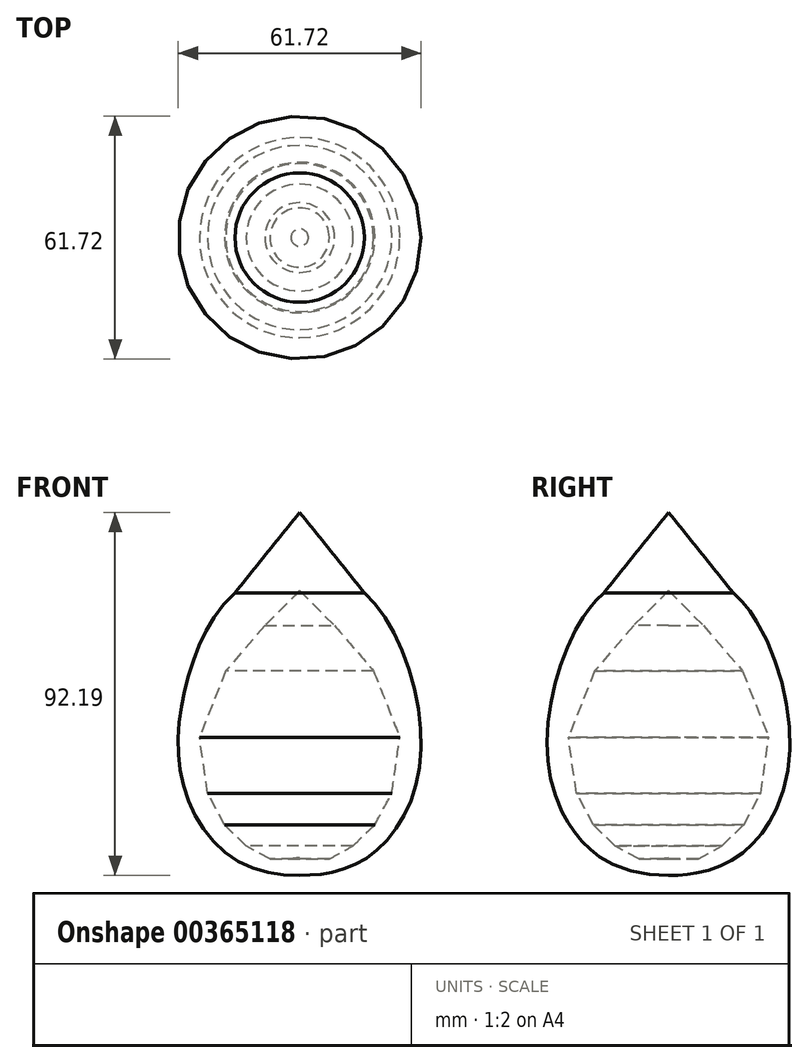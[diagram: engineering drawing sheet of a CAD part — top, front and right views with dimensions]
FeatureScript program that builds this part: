
annotation { "Feature Type Name" : "Feature", "Feature Type Description" : "" }
export const myFeature = defineFeature(function(context is Context, id is Id, definition is map)
    precondition{}
    {
        {
            var Q0;
            Q0=qCreatedBy(makeId("Front.planeOp"),FACE);
            var sketch = newSketch(context, id + "F0", { "sketchPlane" : qUnion([Q0])});
            skFitSpline(sketch, "E0", {"points": [v(-13.57, -42.8) * mm, v(3, -38.67) * mm, v(17.18, -12.44) * mm, v(2.87, 28.92) * mm, v(-13.57, 33.4) * mm], "startDerivative": vector(71.93, -0.04) * mm, "endDerivative": vector(-67.02, -1) * mm});
            skLineSegment(sketch, "E1", {"start": v(-4.72, 20.7) * mm, "end": v(-13.57, 29.55) * mm});
            skLineSegment(sketch, "E2", {"start": v(-13.57, 29.55) * mm, "end": v(-13.57, 33.4) * mm});
            skLineSegment(sketch, "E3", {"start": v(-4.72, 20.7) * mm, "end": v(5.2, 9.15) * mm});
            skLineSegment(sketch, "E4", {"start": v(5.2, 9.15) * mm, "end": v(11.87, -7.69) * mm});
            skLineSegment(sketch, "E5", {"start": v(11.87, -7.69) * mm, "end": v(10.85, -14.84) * mm});
            skLineSegment(sketch, "E6", {"start": v(-13.57, 50.02) * mm, "end": v(-13.57, -55.05) * mm, "construction": true});
            skLineSegment(sketch, "E7", {"start": v(10.85, -14.84) * mm, "end": v(9.84, -21.93) * mm});
            skLineSegment(sketch, "E8", {"start": v(9.84, -21.93) * mm, "end": v(5.52, -29.95) * mm});
            skLineSegment(sketch, "E9", {"start": v(5.52, -29.95) * mm, "end": v(0, -35.28) * mm});
            skLineSegment(sketch, "E10", {"start": v(0, -35.28) * mm, "end": v(-6.03, -38.61) * mm});
            skLineSegment(sketch, "E11", {"start": v(-6.03, -38.61) * mm, "end": v(-11.37, -38.61) * mm});
            skLineSegment(sketch, "E12", {"start": v(-11.37, -38.61) * mm, "end": v(-13.57, -38.3) * mm});
            skLineSegment(sketch, "E13", {"start": v(-13.57, -38.3) * mm, "end": v(-13.57, -42.8) * mm});
            skArc(sketch, "E14", {"start": v(2.87, 28.92) * mm, "mid": v(-5.31, 39.19) * mm, "end": v(-13.57, 49.4) * mm});
            skLineSegment(sketch, "E15", {"start": v(-13.57, 49.4) * mm, "end": v(-13.57, -38.3) * mm});
            skSolve(sketch);
        }
        {
            var Q0;
            {var subQ0=sQuery(id+"F0.wireOp",EDGE,"E15");var subQ1=sQuery(id+"F0.wireOp",EDGE,"E0");var subQ2=makeQuery(id+"F0.imprint","INTERSECT",VERTEX,{"derivedFrom":[subQ1,subQ0]});Q0=makeQuery(id+"F0.imprint","IMPRINT",FACE,{"disambiguationData":[TD([[makeQuery(id+"F0.imprint","IMPRINT",EDGE,{"disambiguationData":[TD([[subQ2,1.0]])],"derivedFrom":subQ1}),-1.0]])]});}
            var Q1;
            {var subQ7=sQuery(id+"F0.wireOp",EDGE,"E1");Q1=makeQuery(id+"F0.imprint","IMPRINT",FACE,{"disambiguationData":[TD([[makeQuery(id+"F0.imprint","IMPRINT",EDGE,{"derivedFrom":subQ7}),-1.0]])]});}
            var Q2;
            Q2=sQuery(id+"F0.wireOp",EDGE,"E6");
            revolve(context, id + "F1", {"entities" : qUnion([Q0, Q1]), "axis" : qUnion([Q2]), "revolveType" : RevolveType.FULL});
        }
    });
